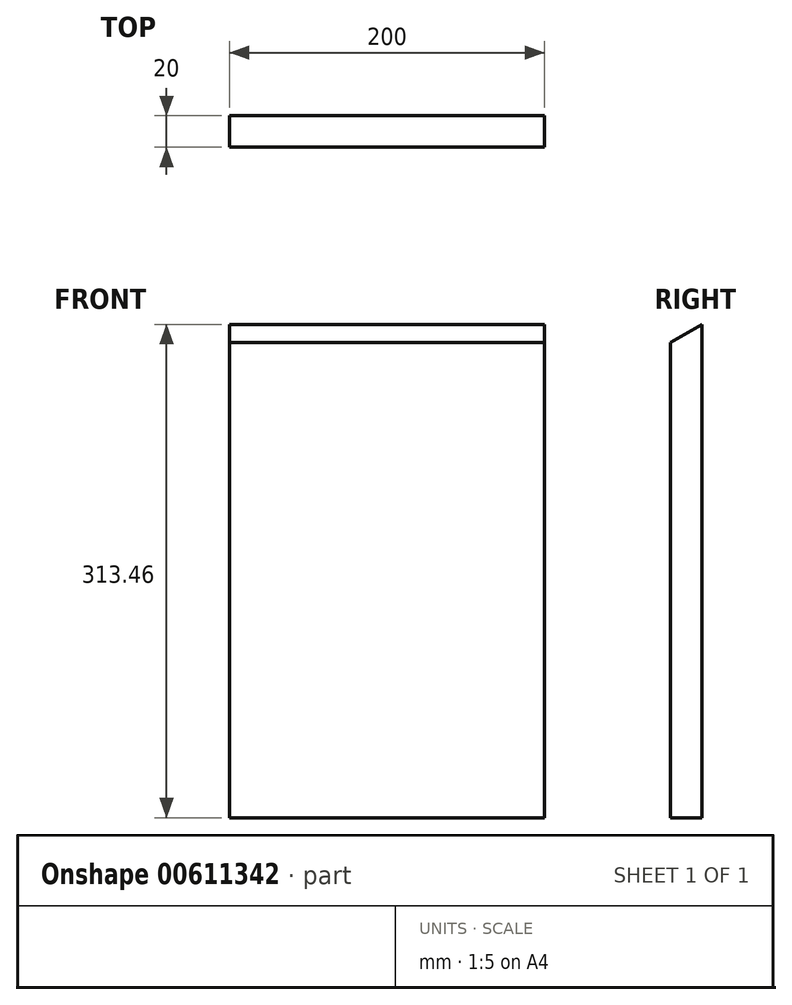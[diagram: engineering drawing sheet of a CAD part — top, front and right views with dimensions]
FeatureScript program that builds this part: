
annotation { "Feature Type Name" : "Feature", "Feature Type Description" : "" }
export const myFeature = defineFeature(function(context is Context, id is Id, definition is map)
    precondition{}
    {
        {
            var Q0;
            Q0=qCreatedBy(makeId("Front.planeOp"),FACE);
            var sketch = newSketch(context, id + "F0", { "sketchPlane" : qUnion([Q0])});
            skLineSegment(sketch, "E0.bottom", {"start": v(-100, 156.73) * mm, "end": v(100, 156.73) * mm});
            skLineSegment(sketch, "E0.top", {"start": v(-100, -156.73) * mm, "end": v(100, -156.73) * mm});
            skLineSegment(sketch, "E0.left", {"start": v(-100, 156.73) * mm, "end": v(-100, -156.73) * mm});
            skLineSegment(sketch, "E0.right", {"start": v(100, 156.73) * mm, "end": v(100, -156.73) * mm});
            skPoint(sketch, "E0.middle", {"position": v(0, 0) * mm});
            skSolve(sketch);
        }
        {
            var Q0;
            Q0=makeQuery(id+"F0.imprint","IMPRINT",FACE,{"disambiguationData":[TD([[makeQuery(id+"F0.imprint","IMPRINT",EDGE,{"derivedFrom":sQuery(id+"F0.wireOp",EDGE,"E0.bottom")}),-1.0]])]});
            extrude(context, id + "F1", {"entities" : qUnion([Q0]), "depth" : 20 * mm, "offsetDistance" : 25 * mm});
        }
        {
            var Q0;
            Q0=makeQuery(id+"F1.opExtrude","SWEPT_FACE",FACE,{"disambiguationData":[OSD([sQuery(id+"F0.wireOp",EDGE,"E0.left")])]});
            var sketch = newSketch(context, id + "F2", { "sketchPlane" : qUnion([Q0])});
            skLineSegment(sketch, "E1", {"start": v(0, 156.73) * mm, "end": v(20, 145.18) * mm});
            skLineSegment(sketch, "E2", {"start": v(20, 145.18) * mm, "end": v(20, 145.18) * mm});
            skLineSegment(sketch, "E3", {"start": v(20, 156.73) * mm, "end": v(20, 156.73) * mm});
            skLineSegment(sketch, "E4", {"start": v(20, 156.73) * mm, "end": v(0, 156.73) * mm});
            skLineSegment(sketch, "E5", {"start": v(20, 145.18) * mm, "end": v(20, 156.73) * mm});
            skSolve(sketch);
        }
        {
            var Q0;
            Q0=makeQuery(id+"F2.imprint","IMPRINT",FACE,{"disambiguationData":[TD([[makeQuery(id+"F2.imprint","IMPRINT",EDGE,{"derivedFrom":sQuery(id+"F2.wireOp",EDGE,"E1")}),1.0]])]});
            extrude(context, id + "F3", {"entities" : qUnion([Q0]), "operationType" : NewBodyOperationType.REMOVE, "endBound" : BoundingType.THROUGH_ALL, "oppositeDirection" : true, "depth" : 25 * mm, "offsetDistance" : 25 * mm});
        }
    });
